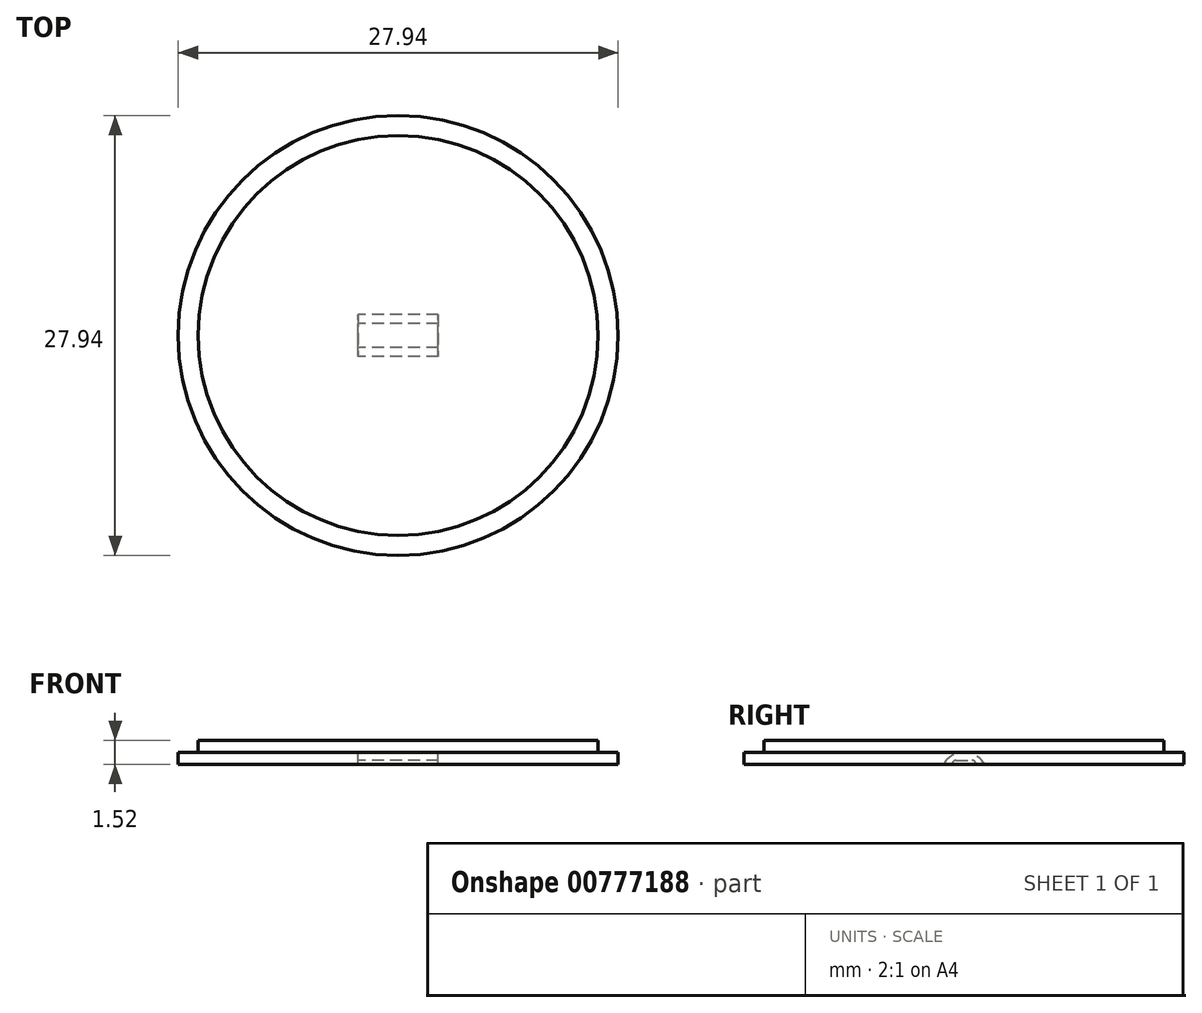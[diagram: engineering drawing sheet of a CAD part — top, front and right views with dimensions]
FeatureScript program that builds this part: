
annotation { "Feature Type Name" : "Feature", "Feature Type Description" : "" }
export const myFeature = defineFeature(function(context is Context, id is Id, definition is map)
    precondition{}
    {
        {
            var Q0;
            Q0=qCreatedBy(makeId("Top.planeOp"),FACE);
            var sketch = newSketch(context, id + "F0", { "sketchPlane" : qUnion([Q0])});
            skCircle(sketch, "E0", {"center": v(0, 0) * mm, "radius": 12.7 * mm});
            skSolve(sketch);
        }
        {
            var Q0;
            Q0=qSketchRegion(id+"F0",true);
            extrude(context, id + "F1", {"entities" : qUnion([Q0]), "depth" : 1.52 * mm, "offsetDistance" : 25.4 * mm});
        }
        {
            var Q0;
            Q0=qCreatedBy(makeId("Top.planeOp"),FACE);
            var sketch = newSketch(context, id + "F2", { "sketchPlane" : qUnion([Q0])});
            skCircle(sketch, "E1", {"center": v(0, 0) * mm, "radius": 13.97 * mm});
            skSolve(sketch);
        }
        {
            var Q0;
            Q0=qSketchRegion(id+"F2",true);
            extrude(context, id + "F3", {"entities" : qUnion([Q0]), "operationType" : NewBodyOperationType.ADD, "depth" : 0.76 * mm, "offsetDistance" : 25.4 * mm});
        }
        {
            var Q0;
            Q0=qCreatedBy(makeId("Front.planeOp"),FACE);
            var sketch = newSketch(context, id + "F4", { "sketchPlane" : qUnion([Q0])});
            skLineSegment(sketch, "E2.bottom", {"start": v(2.54, -0.76) * mm, "end": v(-2.54, -0.76) * mm});
            skLineSegment(sketch, "E2.top", {"start": v(2.54, 0.76) * mm, "end": v(-2.54, 0.76) * mm});
            skLineSegment(sketch, "E2.left", {"start": v(2.54, -0.76) * mm, "end": v(2.54, 0.76) * mm});
            skLineSegment(sketch, "E2.right", {"start": v(-2.54, -0.76) * mm, "end": v(-2.54, 0.76) * mm});
            skPoint(sketch, "E2.middle", {"position": v(0, 0) * mm});
            skSolve(sketch);
        }
        {
            var Q0;
            Q0=qSketchRegion(id+"F4",true);
            var Q1;
            Q1=sQuery(id+"F4.wireOp",EDGE,"E2.bottom");
            revolve(context, id + "F5", {"operationType" : NewBodyOperationType.REMOVE, "surfaceOperationType" : NewSurfaceOperationType.NEW, "entities" : qUnion([Q0]), "axis" : qUnion([Q1]), "revolveType" : RevolveType.FULL, "oppositeDirection" : true});
        }
        {
            var Q0;
            Q0=qCreatedBy(makeId("Top.planeOp"),FACE);
            var sketch = newSketch(context, id + "F6", { "sketchPlane" : qUnion([Q0])});
            skLineSegment(sketch, "E3.bottom", {"start": v(2.54, -0.76) * mm, "end": v(-2.54, -0.76) * mm});
            skLineSegment(sketch, "E3.top", {"start": v(2.54, 0.76) * mm, "end": v(-2.54, 0.76) * mm});
            skLineSegment(sketch, "E3.left", {"start": v(2.54, -0.76) * mm, "end": v(2.54, 0.76) * mm});
            skLineSegment(sketch, "E3.right", {"start": v(-2.54, -0.76) * mm, "end": v(-2.54, 0.76) * mm});
            skPoint(sketch, "E3.middle", {"position": v(0, 0) * mm});
            skSolve(sketch);
        }
        {
            var Q0;
            Q0=qSketchRegion(id+"F6",true);
            extrude(context, id + "F7", {"entities" : qUnion([Q0]), "depth" : 0.25 * mm, "offsetDistance" : 25.4 * mm});
        }
        {
            var Q0;
            Q0=makeQuery(id+"F7.opExtrude","CAP_EDGE",EDGE,{"disambiguationData":[OSD([sQuery(id+"F6.wireOp",EDGE,"E3.top")])],"isStart":false});
            var Q1;
            Q1=makeQuery(id+"F7.opExtrude","CAP_EDGE",EDGE,{"disambiguationData":[OSD([sQuery(id+"F6.wireOp",EDGE,"E3.bottom")])],"isStart":false});
            fillet(context, id + "F8", {"entities" : qUnion([Q0, Q1]), "radius" : 0.25 * mm, "tangentPropagation" : true, "allowEdgeOverflow" : false});
        }
    });
